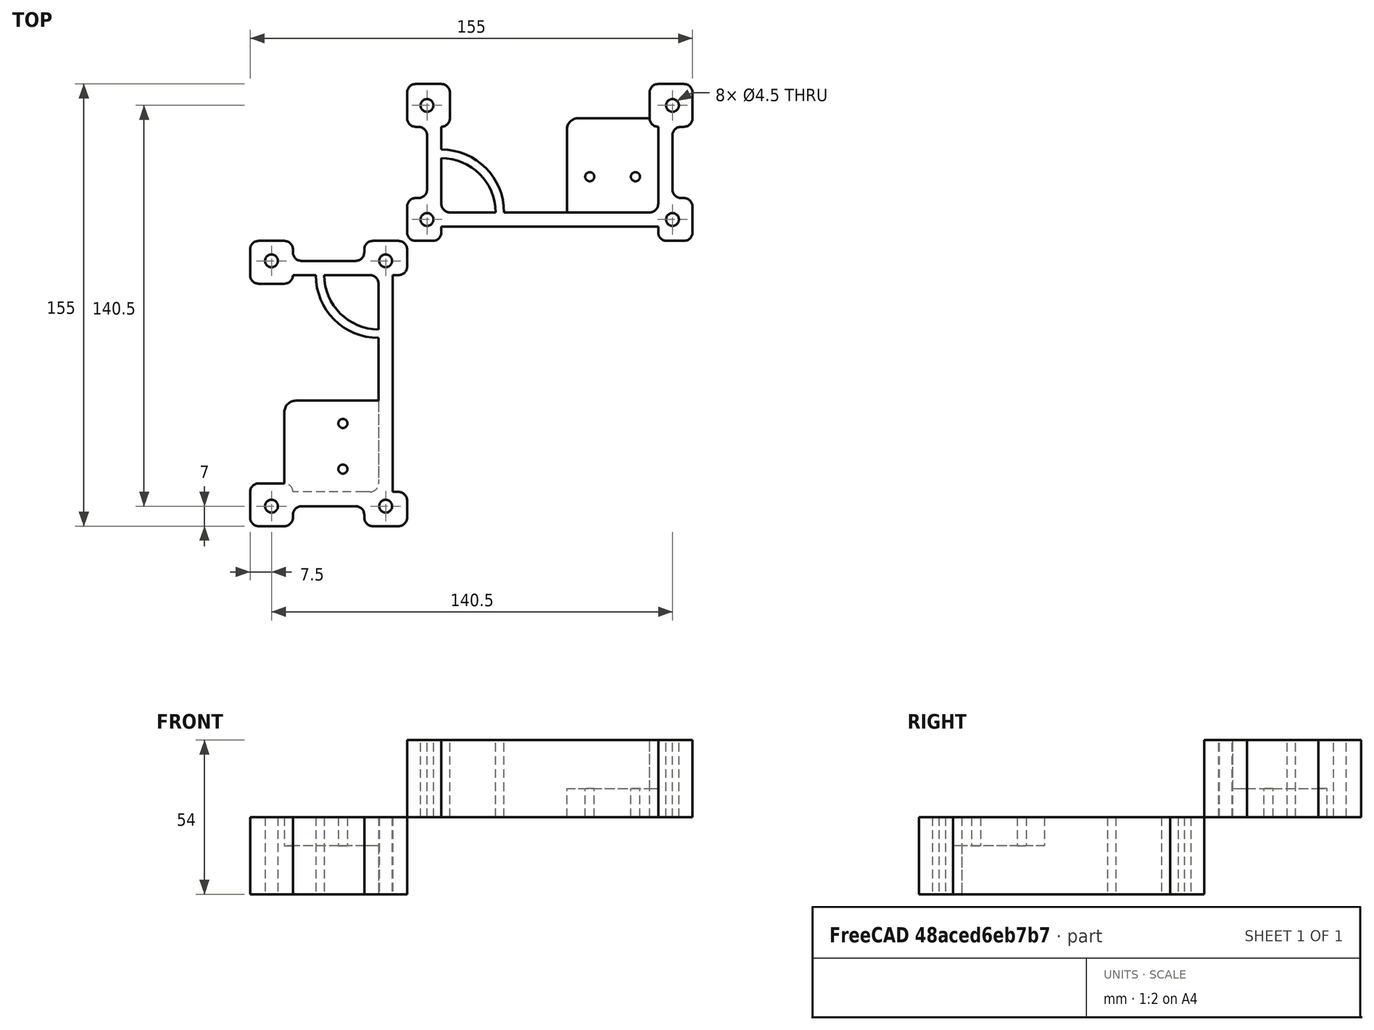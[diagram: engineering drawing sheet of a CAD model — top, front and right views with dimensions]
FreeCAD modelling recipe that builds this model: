
FCSTD DOCUMENT  (FreeCAD 0.15R4630 (Git))
Label: x_tower_left
License: All rights reserved
LicenseURL: http://en.wikipedia.org/wiki/All_rights_reserved
objects: Part::Box×8, Part::Cylinder×8, Part::MultiFuse×7, Part::Fillet×4, Part::Cut×3, Part::Feature×2, Mesh::Feature×1
note: 32 computed .brp shape members not serialized (recipe doc carries the construction recipe); baked Part::Feature solids carry a one-line shape summary decoded from their .brp

FEATURE [Mesh::Feature] towerLeft
FEATURE [Part::Feature] towerLeft001001  label="towerLeft002"
  shape: bbox 100 x 55 x 27 mm, 2727 faces, 0 solids (baked)
FEATURE [Part::Box] Box  label="Cubo"
  Height = 27
  Length = 12
  Width = 15
FEATURE [Part::Box] Box001  label="Cubo001"
  Height = 27
  Length = 12
  Placement = pos=(88,0,0) rot=(0,0,1;0rad)
  Width = 15
FEATURE [Part::Box] Box002  label="Cubo002"
  Height = 27
  Length = 15
  Placement = pos=(85,40,0) rot=(0,0,1;0rad)
  Width = 15
FEATURE [Part::Box] Box003  label="Cubo003"
  Height = 27
  Length = 15
  Placement = pos=(0,40,0) rot=(0,0,1;0rad)
  Width = 15
FEATURE [Part::MultiFuse] Fusion
  Shapes = -> [Box,Box002,Box001,Box003]
FEATURE [Part::Box] Box004  label="Cubo004"
  Height = 27
  Length = 76
  Placement = pos=(12,5,0) rot=(0,0,1;0rad)
  Width = 5
FEATURE [Part::Box] Box005  label="Cubo005"
  Height = 27
  Length = 5
  Placement = pos=(7,15,0) rot=(0,0,1;0rad)
  Width = 25
FEATURE [Part::Box] Box006  label="Cubo006"
  Height = 27
  Length = 5
  Placement = pos=(88,15,0) rot=(0,0,1;0rad)
  Width = 25
FEATURE [Part::MultiFuse] Fusion001
  Shapes = -> [Box005,Box004,Box006]
FEATURE [Part::Box] Box007  label="Cubo007"
  Height = 10
  Length = 32
  Placement = pos=(56,10,0) rot=(0,0,1;0rad)
  Width = 33
FEATURE [Part::Cylinder] Cylinder  label="Cilindro"
  Angle = 90
  Height = 27
  Placement = pos=(12,10,0) rot=(0,0,1;0rad)
  Radius = 22
FEATURE [Part::Cylinder] Cylinder001  label="Cilindro001"
  Angle = 90
  Height = 27
  Placement = pos=(12,10,0) rot=(0,0,1;0rad)
  Radius = 19
FEATURE [Part::Cut] Cut
  Base = -> Cylinder
  Tool = -> Cylinder001
FEATURE [Part::Fillet] Fillet
  Base = -> Fusion
  Edges = 14 edges r=3: [Edge1,Edge3,Edge6,Edge11,Edge13,Edge18,Edge23,Edge25,Edge27,Edge30,Edge37,Edge39,Edge42,Edge47]
FEATURE [Part::MultiFuse] Fusion002
  Shapes = -> [Fusion001,Fillet]
FEATURE [Part::MultiFuse] Fusion003
  Shapes = -> [Box007,Fusion002]
FEATURE [Part::Fillet] Fillet001
  Base = -> Fusion003
  Edges = 2 edges r=3: [Edge61,Edge72]
FEATURE [Part::Fillet] Fillet002
  Base = -> Fillet001
  Edges = 1 edges r=4: [Edge80]
FEATURE [Part::MultiFuse] Fusion004
  Shapes = -> [Fillet002,Cut]
FEATURE [Part::Cylinder] Cylinder002  label="Cilindro002"
  Angle = 360
  Height = 29
  Placement = pos=(7,7.5,-1) rot=(0,0,1;0rad)
  Radius = 2.25
FEATURE [Part::Cylinder] Cylinder003  label="Cilindro003"
  Angle = 360
  Height = 29
  Placement = pos=(7,47.5,-1) rot=(0,0,1;0rad)
  Radius = 2.25
FEATURE [Part::Cylinder] Cylinder004  label="Cilindro004"
  Angle = 360
  Height = 29
  Placement = pos=(93,47.5,-1) rot=(0,0,1;0rad)
  Radius = 2.25
FEATURE [Part::Cylinder] Cylinder005  label="Cilindro005"
  Angle = 360
  Height = 29
  Placement = pos=(93,7.5,-1) rot=(0,0,1;0rad)
  Radius = 2.25
FEATURE [Part::MultiFuse] Fusion005
  Shapes = -> [Cylinder002,Cylinder005,Cylinder004,Cylinder003]
FEATURE [Part::Cut] Cut001
  Base = -> Fusion004
  Tool = -> Fusion005
FEATURE [Part::Cylinder] Cylinder006  label="Cilindro006"
  Angle = 360
  Height = 12
  Placement = pos=(80,22.5,-1) rot=(0,0,1;0rad)
  Radius = 1.6
FEATURE [Part::Cylinder] Cylinder007  label="Cilindro007"
  Angle = 360
  Height = 12
  Placement = pos=(64,22.5,-1) rot=(0,0,1;0rad)
  Radius = 1.6
FEATURE [Part::MultiFuse] Fusion006
  Shapes = -> [Cylinder006,Cylinder007]
FEATURE [Part::Cut] Cut002
  Base = -> Cut001
  Tool = -> Fusion006
FEATURE [Part::Fillet] Fillet003  label="x_tower_left"
  Base = -> Cut002
  Edges = 4 edges r=3: [Edge129,Edge130,Edge149,Edge163]
FEATURE [Part::Feature] Fillet003001  label="x_tower_left001"
  Placement = pos=(0,0,0) rot=(-0.707107,0.707107,0;3.14159rad)
  shape: bbox 55 x 100 x 27 mm, 58 faces (baked)
